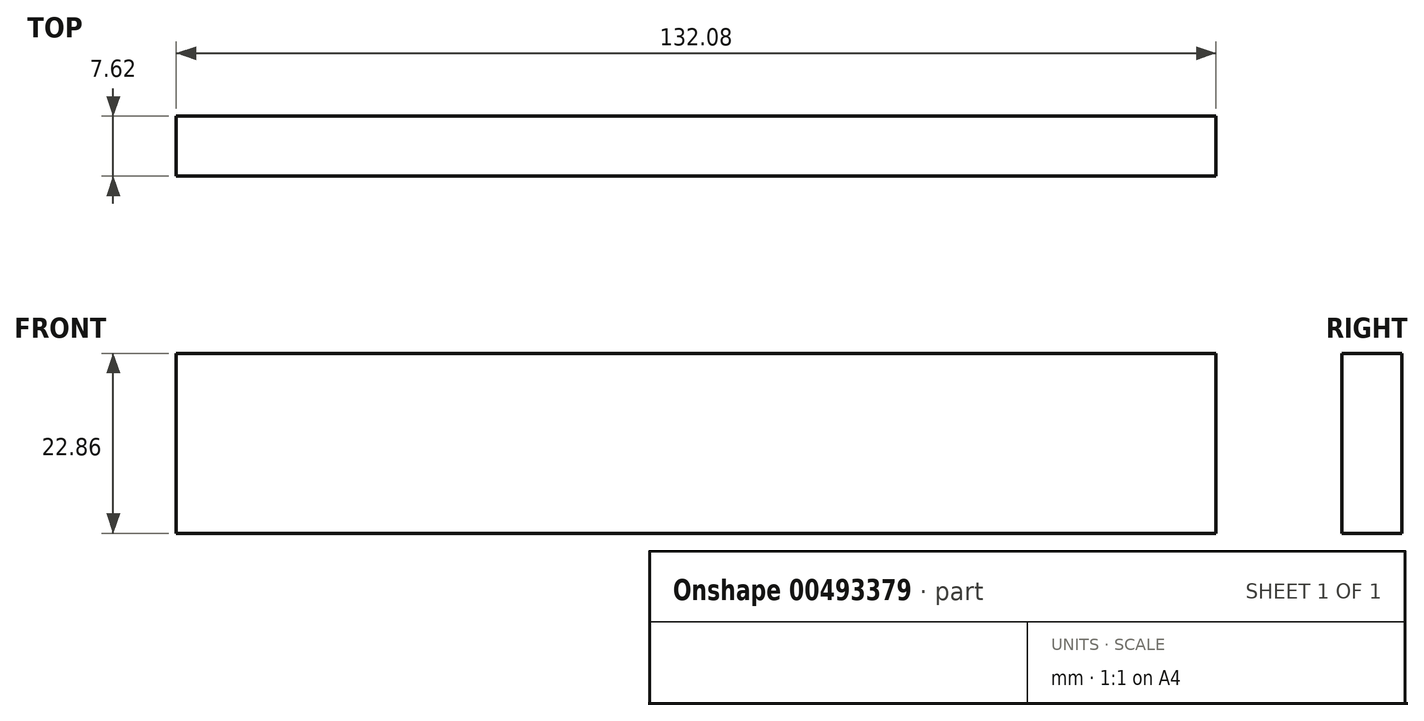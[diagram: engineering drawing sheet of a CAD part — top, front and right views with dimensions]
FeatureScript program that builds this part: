
annotation { "Feature Type Name" : "Feature", "Feature Type Description" : "" }
export const myFeature = defineFeature(function(context is Context, id is Id, definition is map)
    precondition{}
    {
        {
            var Q0;
            Q0=qCreatedBy(makeId("Front.planeOp"),FACE);
            var sketch = newSketch(context, id + "F0", { "sketchPlane" : qUnion([Q0])});
            skLineSegment(sketch, "E0.bottom", {"start": v(66.04, 11.43) * mm, "end": v(-66.04, 11.43) * mm});
            skLineSegment(sketch, "E0.top", {"start": v(66.04, -11.43) * mm, "end": v(-66.04, -11.43) * mm});
            skLineSegment(sketch, "E0.left", {"start": v(66.04, 11.43) * mm, "end": v(66.04, -11.43) * mm});
            skLineSegment(sketch, "E0.right", {"start": v(-66.04, 11.43) * mm, "end": v(-66.04, -11.43) * mm});
            skPoint(sketch, "E0.middle", {"position": v(0, 0) * mm});
            skSolve(sketch);
        }
        {
            var Q0;
            Q0=makeQuery(id+"F0.imprint","IMPRINT",FACE,{"disambiguationData":[TD([[makeQuery(id+"F0.imprint","IMPRINT",EDGE,{"derivedFrom":sQuery(id+"F0.wireOp",EDGE,"E0.bottom")}),1.0]])]});
            extrude(context, id + "F1", {"entities" : qUnion([Q0]), "endBound" : BoundingType.SYMMETRIC, "depth" : 7.62 * mm});
        }
    });
